# Revit family: 0045748
name_source: partatom
category: Lighting Fixtures
revit_build: Autodesk Revit 2017 (Build: 20190507_1515(x64)
units: mm (PartAtom-declared; Revit-internal decimal feet)

## family parameters
Cut with Voids When Loaded = No
Host = Face
Light Source = Yes
OmniClass Number = 23.80.70.00
OmniClass Title = Lighting
Part Type = Normal
Room Calculation Point = No
Round Connector Dimension = Use Diameter
Shared = No

## types (6) — shared parameters
Assembly Code = D5020200
AssetType = Fixed
BRACKET1_END_SYL = 359 mm  [stored 1.17782 ft]
BRACKET1_ST_SYL = 399 mm  [stored 1.30906 ft]
CABLE_D_SYL = 23 mm
ClassificationName = Uniclass2015
ClassificationValue = EF_70_80
Color Filter = 16777215
Default Elevation = 1219 mm
Dimming Lamp Color Temperature Shift = <None>
DocumentationLiterature = http://www.sylvania-lighting.com
ElectricShockClassification = Class II
Emit Shape Visible in Rendering = No
Emit from Circle Diameter = 610 mm
IfcExportAs = IfcLightFixtureType
IfcExportType = IfcLightFixtureType
ImpactProtectionIndex = IK08
IngressProtection = IP65
Keynote = 16500
L3_SYL = 60 mm
LAMP_L1_SYL = 678 mm  [stored 2.22441 ft]
LUM_D1_SYL = 38 mm  [stored 0.124672 ft]
LUM_LENGHT1500_SYL = Yes
L_CABLE_SYL = 47 mm
Lamp = LED
LampColourRenderingIndex = 80
LampMacAdamStep = 5
LampsType = LED
Manufacturer = Feilo Sylvania
ManufacturerName = Feilo Sylvania
Material_1_SYL = <By Category>
Material_2_SYL = <By Category>
Material_3_SYL = <By Category>
Material_4_SYL = <By Category>
PowerFactor = 0.9
Tilt Angle = -90.00°
Type Image = <None>
URL = http://www.sylvania-lighting.com
Voltage = 0 V
zero-valued in all types: BRACKET2_END_SYL, BRACKET2_ST_SYL, Cost, LUM_D2_SYL

## per-type parameters (varying)
| type | Apparent Load | Description | LampColourTemperature | LampNominalLuminous | LightOutputRatio | LuminousEfficacy | Material | Model | ModelNumber | ModelReference | Name | NominalDepth | NominalHeight | NominalLength | Photometric Web File | PowerConsumption | TypeName | Weight |
| 0045751 ST E BATTEN 1500 IP65 3300LM 830 | 23 VA |  | 3000 K | 3300 lm |  | 143 lm/W | pc polycarbonate housing, pc polycarbonate diffuser | START eco Batten 1500 IP65 3300lm 830 | 0045751 | START eco Batten 1500 IP65 3300lm 830 | START eco Batten 1500 IP65 3300lm 830 | 43 mm  [stored 0.141076 ft] | 50 mm  [stored 0.164042 ft] | 1570 mm | 0045751.ies | 23 W | START eco Batten 1500 IP65 3300lm 830 | 9.0 kg |
| 0045748 ST E BATTEN 1200 IP65 2600LM 840 | 18 VA |  | 4000 K | 2600 lm |  | 144 lm/W | pc polycarbonate housing, pc polycarbonate diffuser | START eco Batten 1200 IP65 2600lm 840 | 0045748 | START eco Batten 1200 IP65 2600lm 840 | START eco Batten 1200 IP65 2600lm 840 | 43 mm  [stored 0.141076 ft] | 50 mm  [stored 0.164042 ft] | 1280 mm  [stored 4.19948 ft] | 0045748.ies | 18 W | START eco Batten 1200 IP65 2600lm 840 | 7.8 kg |
| 0045747 ST E BATTEN 1200 IP65 2600LM 830 | 18 VA |  | 3000 K | 2600 lm |  | 144 lm/W | pc polycarbonate housing, pc polycarbonate diffuser | START eco Batten 1200 IP65 2600lm 830 | 0045747 | START eco Batten 1200 IP65 2600lm 830 | START eco Batten 1200 IP65 2600lm 830 | 43 mm  [stored 0.141076 ft] | 50 mm  [stored 0.164042 ft] | 1280 mm  [stored 4.19948 ft] | 0045747.ies | 18 W | START eco Batten 1200 IP65 2600lm 830 | 7.8 kg |
| 0045415 ST E BATTEN NEO 1500 IP65 3200LM 865 ME | 42 VA | The new upgraded Start eco Batten IP65 (upgraded version of Batten LED LINK) is a versatile range of slimline LED waterproof luminaires that provide an ideal solution for interior and exterior applications such as workshops, garages and outdoor covered spaces. The design allows the luminaire to be easily linked to another luminaire through an IP65 rated connector. The product can be a slimline replacement for single and twin 36W/58W fluorescent waterproof battens.Polycarbonate housing and diffuser, 5200 lm, 42 W, 124 lm/W, 4000 K, drive current 270 mA, non dimmable, CRI 80, IP65, IK08, Class II, nominal average lifetime (h): 30000, 1200 mm x 80 mm x 53.6 mm, energy class: A++ A+ A. | 6500 K | 5200 lm | 100 | 124 lm/W |  | START eco Batten NEO 1500 IP65 3200lm 865 ME | 0045415 | START eco Batten NEO 1500 IP65 3200lm 865 ME | START eco Batten NEO 1500 IP65 3200lm 865 ME | 80 mm  [stored 0.262467 ft] | 54 mm | 1200 mm | 0045415.ies | 42 W | START eco Batten NEO 1500 IP65 3200lm 865 ME | 9.132 kg |
| 0045413 ST E BATTEN NEO 1200 IP65 2500LM 865 ME | 18 VA | The new upgraded Start eco Batten IP65 (upgraded version of Batten LED LINK) is a versatile range of slimline LED waterproof luminaires that provide an ideal solution for interior and exterior applications such as workshops, garages and outdoor covered spaces. The design allows the luminaire to be easily linked to another luminaire through an IP65 rated connector. The product can be a slimline replacement for single and twin 36W/58W fluorescent waterproof battens.Polycarbonate housing and diffuser, 3200 lm, 26 W, 123 lm/W, 4000 K, drive current 170 mA, non dimmable, CRI 80, IP65, IK08, Class II, nominal average lifetime (h): 30000, 1500 mm x 42 mm x 52.8 mm, energy class: A++ A+ A. | 6500 K | 2600 lm | 100 | 144 lm/W |  | START eco Batten NEO 1200 IP65 2500lm 865 ME | 0045413 | START eco Batten NEO 1200 IP65 2500lm 865 ME | START eco Batten NEO 1200 IP65 2500lm 865 ME | 44 mm  [stored 0.144357 ft] | 53 mm | 1500 mm  [stored 4.92126 ft] | 0045413.ies | 18 W | START eco Batten NEO 1200 IP65 2500lm 865 ME | 7.284 kg |
| 0045752 ST E BATTEN 1500 IP65 3300LM 840 | 23 VA |  | 4000 K | 3300 lm |  | 143 lm/W | pc polycarbonate housing, pc polycarbonate diffuser | START eco Batten 1500 IP65 3300lm 840 | 0045752 | START eco Batten 1500 IP65 3300lm 840 | START eco Batten 1500 IP65 3300lm 840 | 43 mm  [stored 0.141076 ft] | 50 mm  [stored 0.164042 ft] | 1570 mm | 0045752.ies | 23 W | START eco Batten 1500 IP65 3300lm 840 | 7.2 kg |

note: [stored X ft] marks values corroborated as IEEE doubles in the binary element streams (Revit-internal decimal feet)

## geometry (parser evidence)
native form markers: Sweep x3
no freeform markers — native parametric forms only
